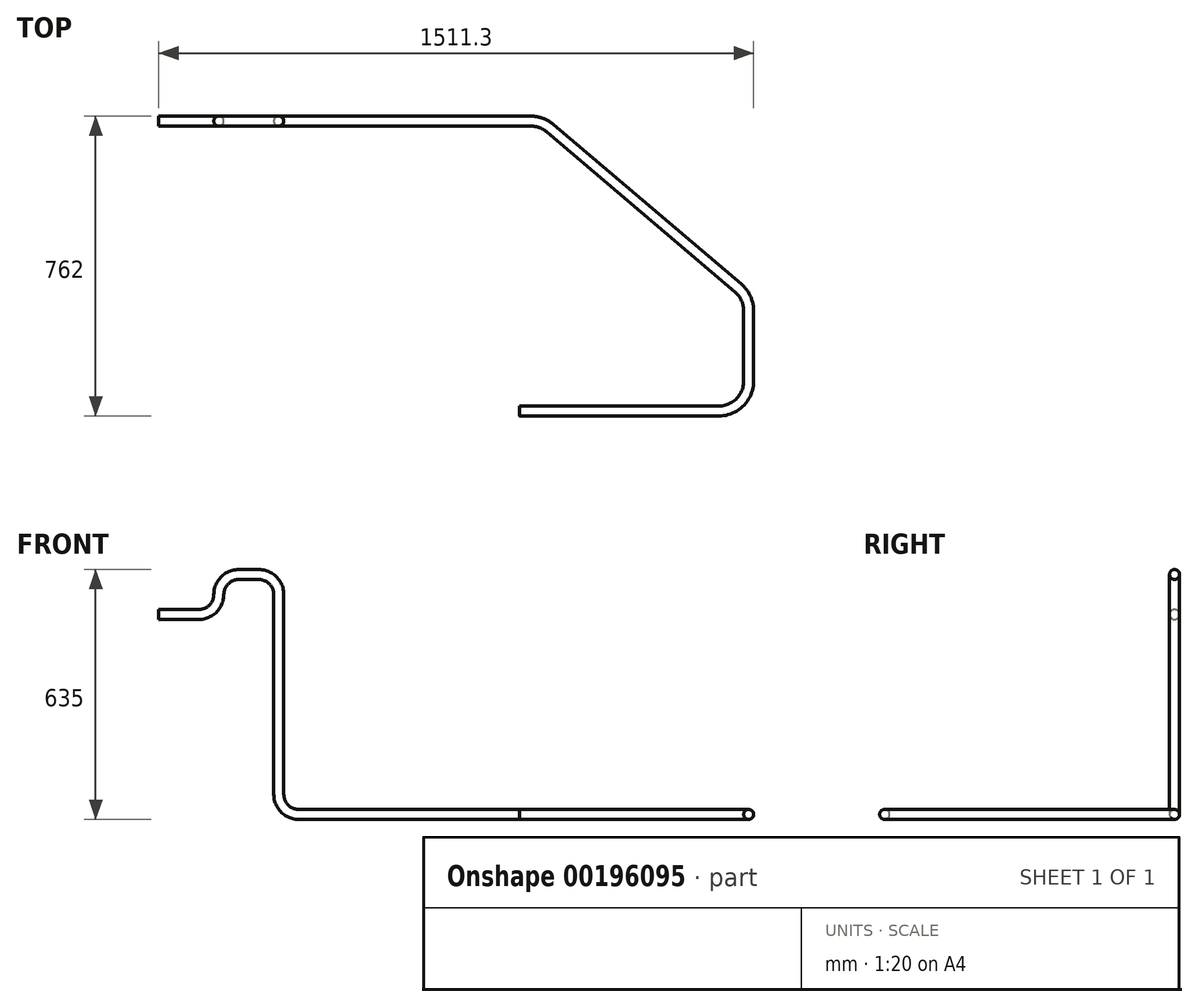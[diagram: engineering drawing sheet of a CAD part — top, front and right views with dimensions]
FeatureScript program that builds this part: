
annotation { "Feature Type Name" : "Feature", "Feature Type Description" : "" }
export const myFeature = defineFeature(function(context is Context, id is Id, definition is map)
    precondition{}
    {
        {
            var Q0;
            Q0=qCreatedBy(makeId("Top.planeOp"),FACE);
            var sketch = newSketch(context, id + "F0", { "sketchPlane" : qUnion([Q0])});
            skLineSegment(sketch, "E0.bottom", {"start": v(0, 0) * mm, "end": v(838.2, 0) * mm, "construction": true});
            skLineSegment(sketch, "E0.top", {"start": v(0, -609.6) * mm, "end": v(838.2, -609.6) * mm, "construction": true});
            skLineSegment(sketch, "E0.left", {"start": v(0, 0) * mm, "end": v(0, -609.6) * mm, "construction": true});
            skLineSegment(sketch, "E0.right", {"start": v(838.2, 0) * mm, "end": v(838.2, -609.6) * mm, "construction": true});
            skLineSegment(sketch, "E1.bottom", {"start": v(838.2, 0) * mm, "end": v(1219.2, 0) * mm, "construction": true});
            skLineSegment(sketch, "E1.top", {"start": v(838.2, -609.6) * mm, "end": v(1219.2, -609.6) * mm, "construction": true});
            skLineSegment(sketch, "E1.right", {"start": v(1219.2, 0) * mm, "end": v(1219.2, -609.6) * mm, "construction": true});
            skPoint(sketch, "E2.firstSnap0", {"position": v(419.1, 0) * mm});
            skLineSegment(sketch, "E2.bottom", {"start": v(1295.4, 0) * mm, "end": v(1905, 0) * mm, "construction": true});
            skLineSegment(sketch, "E2.top", {"start": v(1295.4, -609.6) * mm, "end": v(1905, -609.6) * mm, "construction": true});
            skLineSegment(sketch, "E2.left", {"start": v(1295.4, 0) * mm, "end": v(1295.4, -609.6) * mm, "construction": true});
            skLineSegment(sketch, "E2.right", {"start": v(1905, 0) * mm, "end": v(1905, -609.6) * mm, "construction": true});
            skLineSegment(sketch, "E3.bottom", {"start": v(1295.4, -685.8) * mm, "end": v(1905, -685.8) * mm, "construction": true});
            skLineSegment(sketch, "E3.top", {"start": v(1295.4, -1295.4) * mm, "end": v(1905, -1295.4) * mm, "construction": true});
            skLineSegment(sketch, "E3.left", {"start": v(1295.4, -685.8) * mm, "end": v(1295.4, -1295.4) * mm, "construction": true});
            skLineSegment(sketch, "E3.right", {"start": v(1905, -685.8) * mm, "end": v(1905, -1295.4) * mm, "construction": true});
            skLineSegment(sketch, "E4", {"start": v(1297.3, -838.2) * mm, "end": v(1803.4, -838.2) * mm});
            skLineSegment(sketch, "E5", {"start": v(1879.6, -762) * mm, "end": v(1879.6, -583.97) * mm});
            skPoint(sketch, "E6.visualSharp", {"position": v(1879.6, -838.2) * mm});
            skArc(sketch, "E6.filletArc", {"start": v(1803.4, -838.2) * mm, "mid": v(1857.28, -815.88) * mm, "end": v(1879.6, -762) * mm});
            skLineSegment(sketch, "E7", {"start": v(1325.77, -101.6) * mm, "end": v(736.6, -101.6) * mm});
            skLineSegment(sketch, "E8", {"start": v(1375.13, -119.75) * mm, "end": v(1852.76, -525.92) * mm});
            skPoint(sketch, "E9.visualSharp", {"position": v(1353.79, -101.6) * mm});
            skArc(sketch, "E9.filletArc", {"start": v(1375.13, -119.75) * mm, "mid": v(1352.07, -106.28) * mm, "end": v(1325.77, -101.6) * mm});
            skPoint(sketch, "E10.visualSharp", {"position": v(1879.6, -548.74) * mm});
            skArc(sketch, "E10.filletArc", {"start": v(1879.6, -583.97) * mm, "mid": v(1872.57, -552) * mm, "end": v(1852.76, -525.92) * mm});
            skSolve(sketch);
        }
        {
            var Q0;
            Q0=sQuery(id+"F0.wireOp",VERTEX,"E7.end");
            var Q1;
            Q1=sQuery(id+"F0.wireOp",EDGE,"E7");
            cPlane(context, id + "F1", {"entities" : qUnion([Q0, Q1]), "cplaneType" : CPlaneType.CURVE_POINT, "offset" : 25.4 * mm, "width" : 152.4 * mm, "height" : 152.4 * mm});
        }
        {
            var Q0;
            Q0=qCreatedBy(id+"F1.planeOp",FACE);
            var sketch = newSketch(context, id + "F2", { "sketchPlane" : qUnion([Q0])});
            skCircle(sketch, "E11", {"center": v(101.6, 0) * mm, "radius": 12.7 * mm});
            skSolve(sketch);
        }
        {
            var Q0;
            Q0=makeQuery(id+"F2.imprint","IMPRINT",FACE,{"disambiguationData":[TD([[makeQuery(id+"F2.imprint","IMPRINT",EDGE,{"derivedFrom":sQuery(id+"F2.wireOp",EDGE,"E11")}),1.0]])]});
            var Q1;
            Q1=sQuery(id+"F2.wireOp",EDGE,"E11");
            var Q2;
            Q2=sQuery(id+"F0.wireOp",EDGE,"E7");
            var Q3;
            Q3=sQuery(id+"F0.wireOp",EDGE,"E9.filletArc");
            var Q4;
            Q4=sQuery(id+"F0.wireOp",EDGE,"E8");
            var Q5;
            Q5=sQuery(id+"F0.wireOp",EDGE,"E10.filletArc");
            var Q6;
            Q6=sQuery(id+"F0.wireOp",EDGE,"E5");
            var Q7;
            Q7=sQuery(id+"F0.wireOp",EDGE,"E6.filletArc");
            var Q8;
            Q8=sQuery(id+"F0.wireOp",EDGE,"E4");
            sweep(context, id + "F3", {"profiles" : qUnion([Q0]), "surfaceProfiles" : qUnion([Q1]), "path" : qUnion([Q2, Q3, Q4, Q5, Q6, Q7, Q8])});
        }
        {
            var Q0;
            Q0=sQuery(id+"F0.wireOp",EDGE,"E7");
            cPlane(context, id + "F4", {"entities" : qUnion([Q0]), "cplaneType" : CPlaneType.LINE_ANGLE, "offset" : 25.4 * mm, "angle" : 0 * degree, "width" : 152.4 * mm, "height" : 152.4 * mm});
        }
        {
            var Q0;
            Q0=qCreatedBy(id+"F4.planeOp",FACE);
            var sketch = newSketch(context, id + "F5", { "sketchPlane" : qUnion([Q0])});
            skLineSegment(sketch, "E12", {"start": v(736.6, 0) * mm, "end": v(736.6, 0) * mm});
            skLineSegment(sketch, "E13", {"start": v(685.8, 50.8) * mm, "end": v(685.8, 355.6) * mm});
            skPoint(sketch, "E14.visualSharp", {"position": v(685.8, 0) * mm});
            skArc(sketch, "E14.filletArc", {"start": v(685.8, 50.8) * mm, "mid": v(700.68, 14.88) * mm, "end": v(736.6, 0) * mm});
            skPoint(sketch, "E15.0", {"position": v(736.6, 0) * mm});
            skSolve(sketch);
        }
        {
            var Q0;
            Q0=makeQuery(id+"F3.opSweep","CAP_FACE",FACE,{"disambiguationData":[OSD([sQuery(id+"F0.wireOp",VERTEX,"E7.end"),sQuery(id+"F2.wireOp",EDGE,"E11")])],"isStart":true});
            var Q1;
            Q1=sQuery(id+"F5.wireOp",EDGE,"E14.filletArc");
            var Q2;
            Q2=sQuery(id+"F5.wireOp",EDGE,"E13");
            sweep(context, id + "F6", {"operationType" : NewBodyOperationType.ADD, "profiles" : qUnion([Q0]), "path" : qUnion([Q1, Q2])});
        }
        {
            var Q0;
            Q0=sQuery(id+"F5.wireOp",EDGE,"E13");
            cPlane(context, id + "F7", {"entities" : qUnion([Q0]), "cplaneType" : CPlaneType.LINE_ANGLE, "offset" : 25.4 * mm, "angle" : 90 * degree, "oppositeDirection" : true, "width" : 152.4 * mm, "height" : 152.4 * mm});
        }
        {
            var Q0;
            Q0=qCreatedBy(id+"F7.planeOp",FACE);
            var sketch = newSketch(context, id + "F8", { "sketchPlane" : qUnion([Q0])});
            skLineSegment(sketch, "E16.0", {"start": v(685.8, 50.8) * mm, "end": v(685.8, 355.6) * mm});
            skLineSegment(sketch, "E17", {"start": v(685.8, 355.6) * mm, "end": v(685.8, 558.8) * mm});
            skLineSegment(sketch, "E18", {"start": v(635, 609.6) * mm, "end": v(584.2, 609.6) * mm});
            skPoint(sketch, "E19.visualSharp", {"position": v(685.8, 609.6) * mm});
            skArc(sketch, "E19.filletArc", {"start": v(685.8, 558.8) * mm, "mid": v(670.92, 594.72) * mm, "end": v(635, 609.6) * mm});
            skLineSegment(sketch, "E20", {"start": v(533.4, 558.8) * mm, "end": v(533.4, 558.8) * mm});
            skLineSegment(sketch, "E21", {"start": v(482.6, 508) * mm, "end": v(381, 508) * mm});
            skPoint(sketch, "E22.visualSharp", {"position": v(533.4, 508) * mm});
            skArc(sketch, "E22.filletArc", {"start": v(482.6, 508) * mm, "mid": v(518.52, 522.88) * mm, "end": v(533.4, 558.8) * mm});
            skPoint(sketch, "E23.visualSharp", {"position": v(533.4, 609.6) * mm});
            skArc(sketch, "E23.filletArc", {"start": v(584.2, 609.6) * mm, "mid": v(548.28, 594.72) * mm, "end": v(533.4, 558.8) * mm});
            skSolve(sketch);
        }
        {
            var Q0;
            Q0=makeQuery(id+"F6.opSweep","CAP_FACE",FACE,{"disambiguationData":[OSD([sQuery(id+"F0.wireOp",VERTEX,"E7.end"),sQuery(id+"F2.wireOp",EDGE,"E11"),sQuery(id+"F5.wireOp",VERTEX,"E13.end")])],"isStart":false});
            var Q1;
            Q1=sQuery(id+"F8.wireOp",EDGE,"E19.filletArc");
            var Q2;
            Q2=sQuery(id+"F8.wireOp",EDGE,"E18");
            var Q3;
            Q3=sQuery(id+"F8.wireOp",EDGE,"E17");
            var Q4;
            Q4=sQuery(id+"F8.wireOp",EDGE,"E23.filletArc");
            var Q5;
            Q5=sQuery(id+"F8.wireOp",EDGE,"E20");
            var Q6;
            Q6=sQuery(id+"F8.wireOp",EDGE,"E22.filletArc");
            var Q7;
            Q7=sQuery(id+"F8.wireOp",EDGE,"E21");
            sweep(context, id + "F9", {"operationType" : NewBodyOperationType.ADD, "profiles" : qUnion([Q0]), "path" : qUnion([Q1, Q2, Q3, Q4, Q5, Q6, Q7])});
        }
        {
            var Q0;
            Q0=qCreatedBy(makeId("Top.planeOp"),FACE);
            cPlane(context, id + "F10", {"entities" : qUnion([Q0]), "cplaneType" : CPlaneType.OFFSET, "offset" : 76.2 * mm, "oppositeDirection" : true, "width" : 152.4 * mm, "height" : 152.4 * mm});
        }
    });
